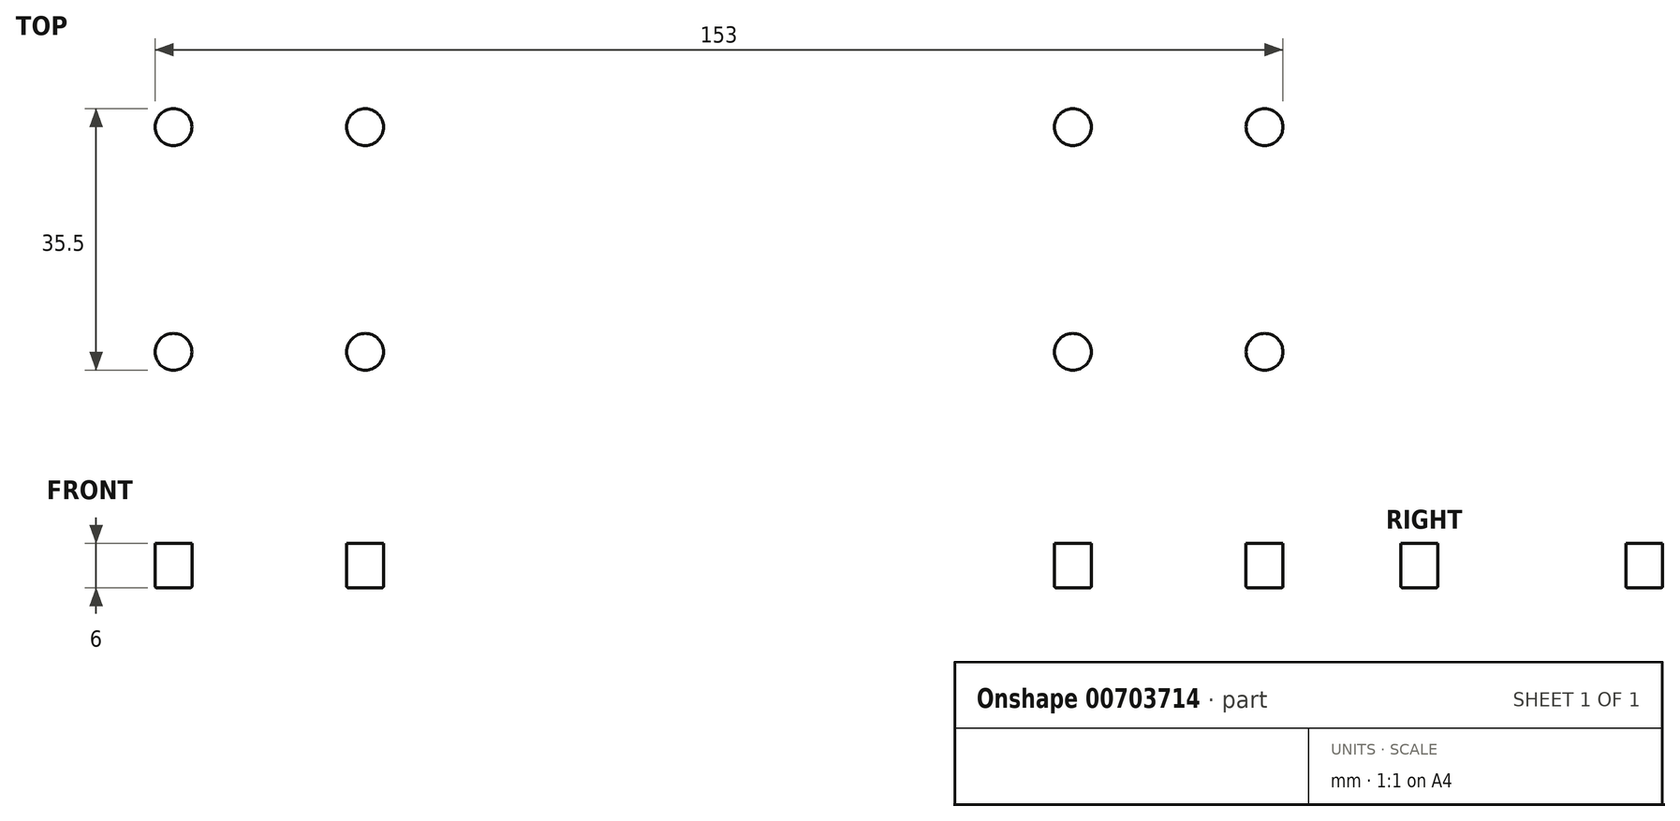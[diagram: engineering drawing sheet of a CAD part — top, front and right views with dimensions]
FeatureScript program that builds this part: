
annotation { "Feature Type Name" : "Feature", "Feature Type Description" : "" }
export const myFeature = defineFeature(function(context is Context, id is Id, definition is map)
    precondition{}
    {
        {
            var Q0;
            Q0=qCreatedBy(makeId("Top.planeOp"),FACE);
            var sketch = newSketch(context, id + "F0", { "sketchPlane" : qUnion([Q0])});
            skLineSegment(sketch, "E0.bottom", {"start": v(-73.95, 22.73) * mm, "end": v(86.05, 22.73) * mm});
            skLineSegment(sketch, "E0.top", {"start": v(-73.95, -19.27) * mm, "end": v(86.05, -19.27) * mm});
            skLineSegment(sketch, "E0.left", {"start": v(-73.95, 22.73) * mm, "end": v(-73.95, -19.27) * mm});
            skLineSegment(sketch, "E0.right", {"start": v(86.05, 22.73) * mm, "end": v(86.05, -19.27) * mm});
            skSolve(sketch);
        }
        {
            var Q0;
            Q0=makeQuery(id+"F0.imprint","IMPRINT",FACE,{"disambiguationData":[TD([[makeQuery(id+"F0.imprint","IMPRINT",EDGE,{"derivedFrom":sQuery(id+"F0.wireOp",EDGE,"E0.bottom")}),-1.0]])]});
            extrude(context, id + "F1", {"entities" : qUnion([Q0]), "depth" : 6 * mm, "offsetDistance" : 25 * mm});
        }
        {
            var Q0;
            Q0=makeQuery(id+"F1.opExtrude","CAP_FACE",FACE,{"disambiguationData":[OSD([sQuery(id+"F0.wireOp",EDGE,"E0.bottom"),sQuery(id+"F0.wireOp",EDGE,"E0.top"),sQuery(id+"F0.wireOp",EDGE,"E0.left"),sQuery(id+"F0.wireOp",EDGE,"E0.right")])],"isStart":false});
            var sketch = newSketch(context, id + "F2", { "sketchPlane" : qUnion([Q0])});
            skCircle(sketch, "E1.0", {"center": v(-67.95, 16.98) * mm, "radius": 2.5 * mm});
            skCircle(sketch, "E2.0", {"center": v(-41.95, 16.98) * mm, "radius": 2.5 * mm});
            skCircle(sketch, "E3.0", {"center": v(-67.95, -13.52) * mm, "radius": 2.5 * mm});
            skCircle(sketch, "E4.0", {"center": v(-41.95, -13.52) * mm, "radius": 2.5 * mm});
            skLineSegment(sketch, "E5", {"start": v(-67.95, 16.98) * mm, "end": v(-67.95, 22.73) * mm, "construction": true});
            skLineSegment(sketch, "E6", {"start": v(-67.95, -13.52) * mm, "end": v(-67.95, -19.27) * mm, "construction": true});
            skCircle(sketch, "E7.0", {"center": v(54.05, 16.98) * mm, "radius": 2.5 * mm});
            skCircle(sketch, "E8.0", {"center": v(80.05, 16.98) * mm, "radius": 2.5 * mm});
            skCircle(sketch, "E9.0", {"center": v(54.05, -13.52) * mm, "radius": 2.5 * mm});
            skCircle(sketch, "E10.0", {"center": v(80.05, -13.52) * mm, "radius": 2.5 * mm});
            skLineSegment(sketch, "E11", {"start": v(54.05, 16.98) * mm, "end": v(54.05, 26.98) * mm, "construction": true});
            skLineSegment(sketch, "E12", {"start": v(54.05, -13.52) * mm, "end": v(54.05, -23.52) * mm, "construction": true});
            skLineSegment(sketch, "E13", {"start": v(-67.95, 16.98) * mm, "end": v(-73.95, 16.98) * mm, "construction": true});
            skLineSegment(sketch, "E14", {"start": v(80.05, 16.98) * mm, "end": v(86.05, 16.98) * mm, "construction": true});
            skSolve(sketch);
        }
        {
            var Q0;
            Q0=makeQuery(id+"F2.imprint","IMPRINT",FACE,{"disambiguationData":[TD([[makeQuery(id+"F2.imprint","IMPRINT",EDGE,{"derivedFrom":sQuery(id+"F2.wireOp",EDGE,"E1.0")}),-1.0]])]});
            var Q1;
            Q1=makeQuery(id+"F2.imprint","IMPRINT",FACE,{"disambiguationData":[TD([[makeQuery(id+"F2.imprint","IMPRINT",EDGE,{"derivedFrom":sQuery(id+"F2.wireOp",EDGE,"E2.0")}),-1.0]])]});
            var Q2;
            Q2=makeQuery(id+"F2.imprint","IMPRINT",FACE,{"disambiguationData":[TD([[makeQuery(id+"F2.imprint","IMPRINT",EDGE,{"derivedFrom":sQuery(id+"F2.wireOp",EDGE,"E7.0")}),-1.0]])]});
            var Q3;
            Q3=makeQuery(id+"F2.imprint","IMPRINT",FACE,{"disambiguationData":[TD([[makeQuery(id+"F2.imprint","IMPRINT",EDGE,{"derivedFrom":sQuery(id+"F2.wireOp",EDGE,"E8.0")}),-1.0]])]});
            var Q4;
            Q4=makeQuery(id+"F2.imprint","IMPRINT",FACE,{"disambiguationData":[TD([[makeQuery(id+"F2.imprint","IMPRINT",EDGE,{"derivedFrom":sQuery(id+"F2.wireOp",EDGE,"E10.0")}),-1.0]])]});
            var Q5;
            Q5=makeQuery(id+"F2.imprint","IMPRINT",FACE,{"disambiguationData":[TD([[makeQuery(id+"F2.imprint","IMPRINT",EDGE,{"derivedFrom":sQuery(id+"F2.wireOp",EDGE,"E9.0")}),-1.0]])]});
            var Q6;
            Q6=makeQuery(id+"F2.imprint","IMPRINT",FACE,{"disambiguationData":[TD([[makeQuery(id+"F2.imprint","IMPRINT",EDGE,{"derivedFrom":sQuery(id+"F2.wireOp",EDGE,"E4.0")}),-1.0]])]});
            var Q7;
            Q7=makeQuery(id+"F2.imprint","IMPRINT",FACE,{"disambiguationData":[TD([[makeQuery(id+"F2.imprint","IMPRINT",EDGE,{"derivedFrom":sQuery(id+"F2.wireOp",EDGE,"E3.0")}),-1.0]])]});
            extrude(context, id + "F3", {"entities" : qUnion([Q0, Q1, Q2, Q3, Q4, Q5, Q6, Q7]), "operationType" : NewBodyOperationType.REMOVE, "endBound" : BoundingType.THROUGH_ALL, "oppositeDirection" : true, "depth" : 25 * mm, "offsetDistance" : 25 * mm});
        }
        {
            var Q0;
            Q0=makeQuery(id+"F0.imprint","IMPRINT",FACE,{"disambiguationData":[TD([[makeQuery(id+"F0.imprint","IMPRINT",EDGE,{"derivedFrom":sQuery(id+"F0.wireOp",EDGE,"E0.bottom")}),-1.0]])]});
            var sketch = newSketch(context, id + "F4", { "sketchPlane" : qUnion([Q0])});
            skLineSegment(sketch, "E15.0.0", {"start": v(86.05, 22.73) * mm, "end": v(-73.95, 22.73) * mm});
            skLineSegment(sketch, "E15.0.1", {"start": v(-73.95, 22.73) * mm, "end": v(-73.95, -19.27) * mm});
            skLineSegment(sketch, "E15.0.2", {"start": v(-73.95, -19.27) * mm, "end": v(86.05, -19.27) * mm});
            skLineSegment(sketch, "E15.0.3", {"start": v(86.05, -19.27) * mm, "end": v(86.05, 22.73) * mm});
            skLineSegment(sketch, "E16", {"start": v(6.05, 22.73) * mm, "end": v(6.05, -19.27) * mm, "construction": true});
            skPoint(sketch, "E17.0", {"position": v(86.05, 1.73) * mm});
            skLineSegment(sketch, "E18", {"start": v(-73.95, 1.73) * mm, "end": v(86.05, 1.73) * mm, "construction": true});
            skCircle(sketch, "E19", {"center": v(-23.95, 11.73) * mm, "radius": 2.5 * mm});
            skCircle(sketch, "E20", {"center": v(-23.95, -8.27) * mm, "radius": 2.5 * mm});
            skCircle(sketch, "E21", {"center": v(-3.95, 11.73) * mm, "radius": 2.5 * mm});
            skCircle(sketch, "E22", {"center": v(-3.95, -8.29) * mm, "radius": 2.5 * mm});
            skCircle(sketch, "E23", {"center": v(36.05, 11.73) * mm, "radius": 2.5 * mm});
            skCircle(sketch, "E24", {"center": v(36.05, -8.27) * mm, "radius": 2.5 * mm});
            skCircle(sketch, "E25", {"center": v(16.05, 11.73) * mm, "radius": 2.5 * mm});
            skCircle(sketch, "E26", {"center": v(16.05, -8.29) * mm, "radius": 2.5 * mm});
            skSolve(sketch);
        }
        {
            var Q0;
            Q0=makeQuery(id+"F4.imprint","IMPRINT",FACE,{"disambiguationData":[TD([[makeQuery(id+"F4.imprint","IMPRINT",EDGE,{"derivedFrom":sQuery(id+"F4.wireOp",EDGE,"E20")}),1.0]])]});
            var Q1;
            Q1=makeQuery(id+"F4.imprint","IMPRINT",FACE,{"disambiguationData":[TD([[makeQuery(id+"F4.imprint","IMPRINT",EDGE,{"derivedFrom":sQuery(id+"F4.wireOp",EDGE,"E19")}),1.0]])]});
            var Q2;
            Q2=makeQuery(id+"F4.imprint","IMPRINT",FACE,{"disambiguationData":[TD([[makeQuery(id+"F4.imprint","IMPRINT",EDGE,{"derivedFrom":sQuery(id+"F4.wireOp",EDGE,"E21")}),1.0]])]});
            var Q3;
            Q3=makeQuery(id+"F4.imprint","IMPRINT",FACE,{"disambiguationData":[TD([[makeQuery(id+"F4.imprint","IMPRINT",EDGE,{"derivedFrom":sQuery(id+"F4.wireOp",EDGE,"E22")}),1.0]])]});
            var Q4;
            Q4=makeQuery(id+"F4.imprint","IMPRINT",FACE,{"disambiguationData":[TD([[makeQuery(id+"F4.imprint","IMPRINT",EDGE,{"derivedFrom":sQuery(id+"F4.wireOp",EDGE,"E26")}),1.0]])]});
            var Q5;
            Q5=makeQuery(id+"F4.imprint","IMPRINT",FACE,{"disambiguationData":[TD([[makeQuery(id+"F4.imprint","IMPRINT",EDGE,{"derivedFrom":sQuery(id+"F4.wireOp",EDGE,"E25")}),1.0]])]});
            var Q6;
            Q6=makeQuery(id+"F4.imprint","IMPRINT",FACE,{"disambiguationData":[TD([[makeQuery(id+"F4.imprint","IMPRINT",EDGE,{"derivedFrom":sQuery(id+"F4.wireOp",EDGE,"E23")}),1.0]])]});
            var Q7;
            Q7=makeQuery(id+"F4.imprint","IMPRINT",FACE,{"disambiguationData":[TD([[makeQuery(id+"F4.imprint","IMPRINT",EDGE,{"derivedFrom":sQuery(id+"F4.wireOp",EDGE,"E24")}),1.0]])]});
            extrude(context, id + "F5", {"entities" : qUnion([Q0, Q1, Q2, Q3, Q4, Q5, Q6, Q7]), "operationType" : NewBodyOperationType.REMOVE, "endBound" : BoundingType.THROUGH_ALL, "depth" : 25 * mm, "offsetDistance" : 25 * mm});
        }
        {
            var Q0;
            Q0=makeQuery(id+"F1.opExtrude","CAP_EDGE",EDGE,{"disambiguationData":[OSD([sQuery(id+"F0.wireOp",EDGE,"E0.bottom")])],"isStart":true});
            var Q1;
            Q1=makeQuery(id+"F1.opExtrude","CAP_FACE",FACE,{"disambiguationData":[OSD([sQuery(id+"F0.wireOp",EDGE,"E0.bottom"),sQuery(id+"F0.wireOp",EDGE,"E0.top"),sQuery(id+"F0.wireOp",EDGE,"E0.left"),sQuery(id+"F0.wireOp",EDGE,"E0.right")])],"isStart":true});
            fillet(context, id + "F6", {"entities" : qUnion([Q0, Q1]), "radius" : .2 * mm, "allowEdgeOverflow" : false});
        }
    });
